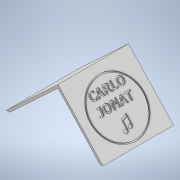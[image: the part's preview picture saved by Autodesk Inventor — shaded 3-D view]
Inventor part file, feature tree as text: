
AUTODESK INVENTOR PART (.ipt)
format: ipt  version: 2022.5 (Build 265521000, 521)  size: 391,168 bytes
history: native  units: mm
features: extrude x2, sketch x2, other x1, projected_geometry x1
ambient origin geometry x8: Origin, YZ Plane, XZ Plane, XY Plane, X Axis, Y Axis, Z Axis, Center Point
bodies: Body1 (feature_tree)
feature tree (6):
  other  "Sólido1"
  extrude  "Extrusión1"  Depth=300.0mm
  extrude  "Extrusión2"  Depth=5.0mm
  sketch  "Boceto1"  dims[d0=280.0mm d1=300.0mm]
  sketch  "Boceto2"  dims[d2=10.0mm d3=10.0mm d4=350.0mm d5=600.0mm d6=0.0mm d7=300.0mm d8=0.0mm d9=220.0mm d10=180.0mm d11=160.0mm d12=230.0mm d13=5.0mm d14=0.0mm]
  projected_geometry  "Contorno proyectado1"
